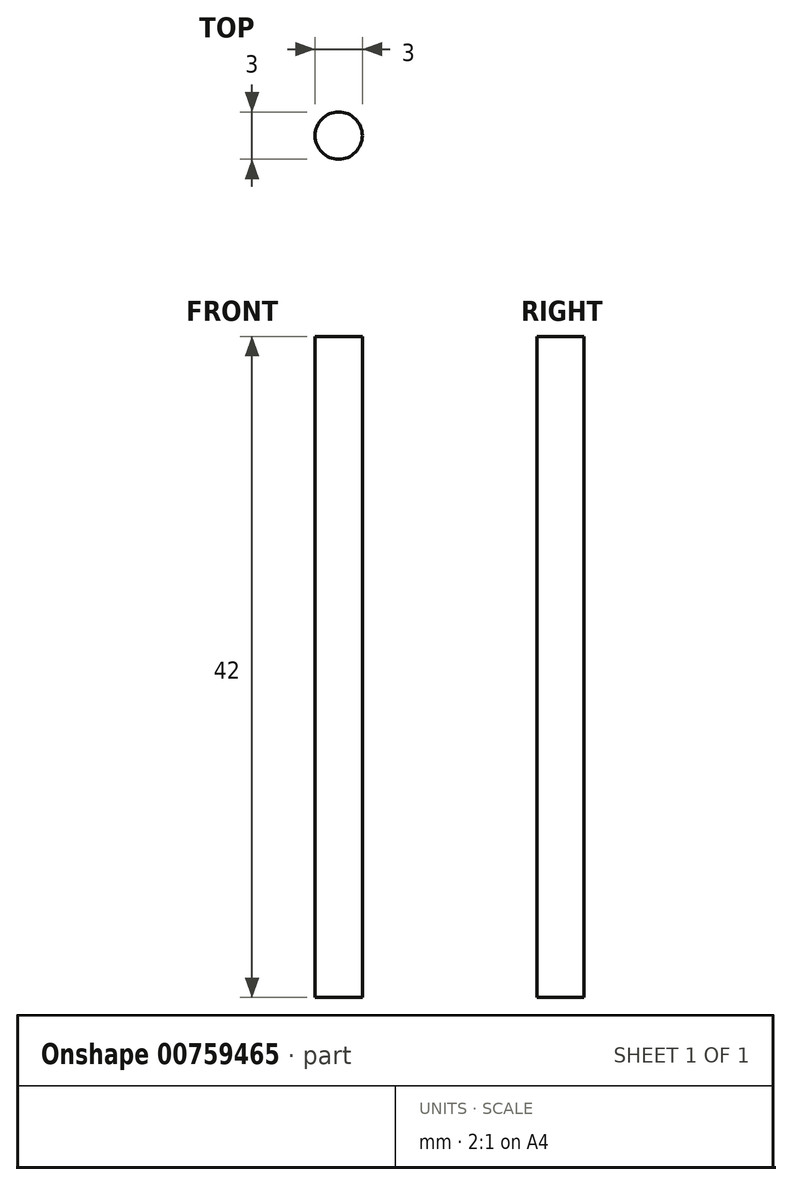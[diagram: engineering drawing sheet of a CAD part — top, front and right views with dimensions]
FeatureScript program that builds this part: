
annotation { "Feature Type Name" : "Feature", "Feature Type Description" : "" }
export const myFeature = defineFeature(function(context is Context, id is Id, definition is map)
    precondition{}
    {
        {
            var Q0;
            Q0=qCreatedBy(makeId("Top.planeOp"),FACE);
            var sketch = newSketch(context, id + "F0", { "sketchPlane" : qUnion([Q0])});
            skCircle(sketch, "E0", {"center": v(0, 0) * mm, "radius": 1.5 * mm});
            skSolve(sketch);
        }
        {
            var Q0;
            Q0 = qSketchRegion(id + "F0", true);
            extrude(context, id + "F1", {"entities" : qUnion([Q0]), "oppositeDirection" : true, "depth" : 42 * mm, "offsetDistance" : 25 * mm});
        }
    });
